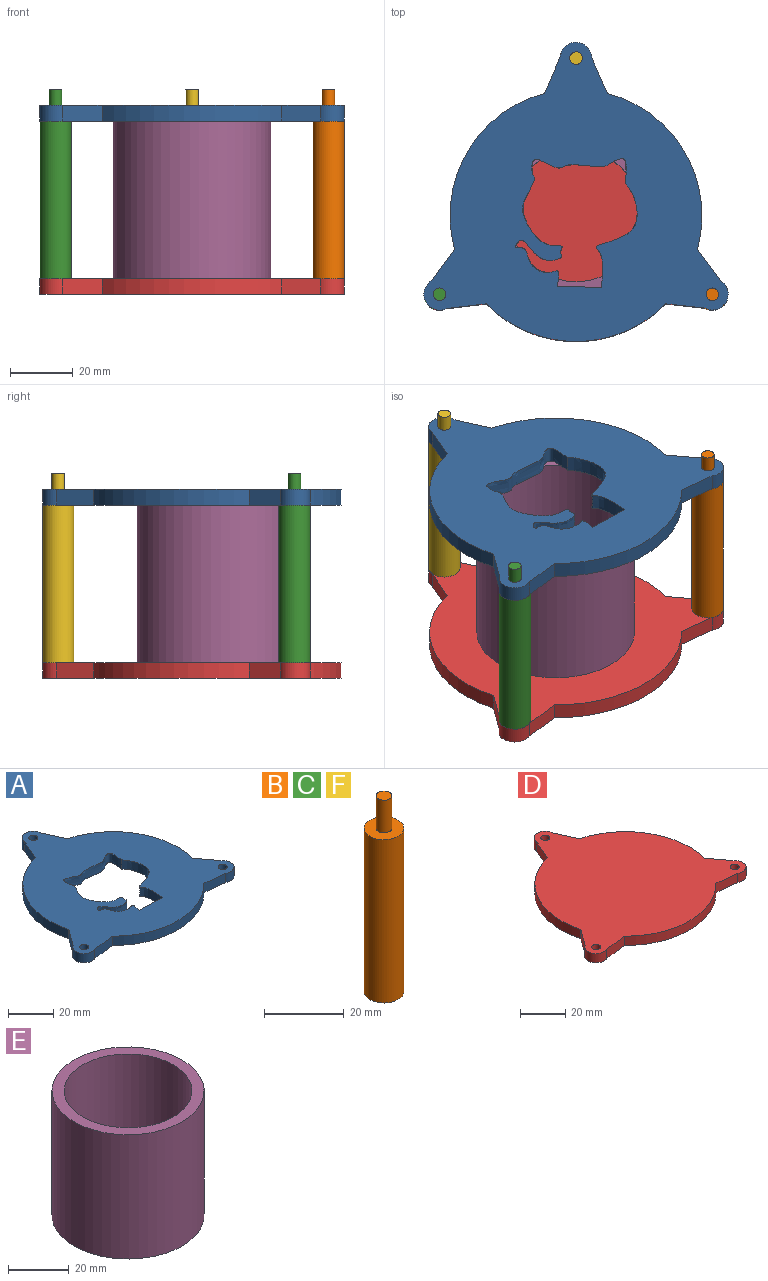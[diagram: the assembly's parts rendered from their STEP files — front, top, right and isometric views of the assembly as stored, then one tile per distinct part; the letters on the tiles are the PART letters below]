
ASSEMBLY  parts=6 mates=4
PART A: 20 faces, bbox 96.6x95x5 mm
  f0: plane 10x7.32mm, normal (-0.81,0.59,0), area 62mm2, adj f1,f17,f18,f19
  f1: cylinder r=5mm len=9.3mm, axis (0,0,-1), area 76.1mm2, adj f0,f2,f18,f19
  f2: plane 12.63x5mm, normal (0.12,-0.99,0), area 63.6mm2, adj f1,f3,f18,f19
  f3: cylinder r=40mm len=57.08mm, axis (0,0,-1), area 317.8mm2, adj f2,f4,f18,f19
  f4: plane 12.32x5mm, normal (-0.11,-0.99,0), area 62mm2, adj f3,f5,f18,f19
  f5: cylinder r=5mm len=9.11mm, axis (0,0,-1), area 76.1mm2, adj f4,f6,f18,f19
  f6: plane 10.19x7.62mm, normal (0.8,0.6,0), area 63.6mm2, adj f5,f7,f18,f19
  f7: cylinder r=40mm len=49.43mm, axis (0,0,-1), area 317.8mm2, adj f6,f8,f18,f19
  f8: plane 11.34x5mm, normal (0.91,0.4,0), area 62mm2, adj f7,f9,f18,f19
  f9: cylinder r=5mm len=9.98mm, axis (0,0,-1), area 76.1mm2, adj f8,f10,f18,f19
  f10: plane 11.69x5.02mm, normal (-0.92,0.39,0), area 63.6mm2, adj f9,f17,f18,f19
  f11: plane 14.05x5mm, normal (0.03,1,0), area 70.3mm2, adj f12,f16,f18,f19
  f12: extruded ~40.51x35.05mm, area 564.8mm2, adj f11,f16,f18,f19
  f13: cylinder r=2mm len=5mm, axis (0,0,-1), area 62.8mm2, adj f18,f19
  f14: cylinder r=2mm len=5mm, axis (0,0,-1), area 62.8mm2, adj f18,f19
  f15: cylinder r=2mm len=5mm, axis (0,0,-1), area 62.8mm2, adj f18,f19
  f16: extruded ~33.22x12.98mm, area 212.8mm2, adj f11,f12,f18,f19
  f17: cylinder r=40mm len=49.43mm, axis (0,0,-1), area 317.8mm2, adj f0,f10,f18,f19
  f18: plane 96.6x95mm, normal (0,0,1), area 4531.6mm2, adj f0,f1,f2,f3,f4,f5,f6,f7
  f19: plane 96.6x95mm, normal (0,0,-1), area 4531.6mm2, adj f0,f1,f2,f3,f4,f5,f6,f7
PART B: 7 faces, bbox 10x10x60 mm
  f0: cylinder r=5mm len=50mm, axis (0,0,-1), area 1570.8mm2, adj f1,f2
  f1: plane 10x10mm, normal (0,0,1), area 66mm2, adj f0,f3
  f2: plane 10x10mm, normal (0,0,-1), area 66mm2, adj f0,f5
  f3: cylinder r=2mm len=10mm, axis (0,0,-1), area 125.7mm2, adj f1,f4
  f4: plane 4x4mm, normal (0,0,1), area 12.6mm2, adj f3
  f5: cylinder r=2mm len=15mm, axis (0,0,-1), area 188.5mm2, adj f2,f6
  f6: plane 4x4mm, normal (0,0,-1), area 12.6mm2, adj f5
PART C: same geometry as B
PART D: 17 faces, bbox 96.6x95x5 mm
  f0: plane 10x7.32mm, normal (-0.81,0.59,0), area 62mm2, adj f1,f14,f15,f16
  f1: cylinder r=5mm len=9.3mm, axis (0,0,-1), area 76.1mm2, adj f0,f2,f15,f16
  f2: plane 12.63x5mm, normal (0.12,-0.99,0), area 63.6mm2, adj f1,f3,f15,f16
  f3: cylinder r=40mm len=57.08mm, axis (0,0,-1), area 317.8mm2, adj f2,f4,f15,f16
  f4: plane 12.32x5mm, normal (-0.11,-0.99,0), area 62mm2, adj f3,f5,f15,f16
  f5: cylinder r=5mm len=9.11mm, axis (0,0,-1), area 76.1mm2, adj f4,f6,f15,f16
  f6: plane 10.19x7.62mm, normal (0.8,0.6,0), area 63.6mm2, adj f5,f7,f15,f16
  f7: cylinder r=40mm len=49.43mm, axis (0,0,-1), area 317.8mm2, adj f6,f8,f15,f16
  f8: plane 11.34x5mm, normal (0.91,0.4,0), area 62mm2, adj f7,f9,f15,f16
  f9: cylinder r=5mm len=9.98mm, axis (0,0,-1), area 76.1mm2, adj f8,f10,f15,f16
  f10: plane 11.69x5.02mm, normal (-0.92,0.39,0), area 63.6mm2, adj f9,f14,f15,f16
  f11: cylinder r=2mm len=5mm, axis (0,0,-1), area 62.8mm2, adj f15,f16
  f12: cylinder r=2mm len=5mm, axis (0,0,-1), area 62.8mm2, adj f15,f16
  f13: cylinder r=2mm len=5mm, axis (0,0,-1), area 62.8mm2, adj f15,f16
  f14: cylinder r=40mm len=49.43mm, axis (0,0,-1), area 317.8mm2, adj f0,f10,f15,f16
  f15: plane 96.6x95mm, normal (0,0,1), area 5566.2mm2, adj f0,f1,f2,f3,f4,f5,f6,f7
  f16: plane 96.6x95mm, normal (0,0,-1), area 5566.2mm2, adj f0,f1,f2,f3,f4,f5,f6,f7
PART E: 4 faces, bbox 50x50x50 mm
  f0: cylinder r=21mm len=50mm, axis (0,0,-1), area 6597.3mm2, adj f2,f3
  f1: cylinder r=25mm len=50mm, axis (0,0,-1), area 7854mm2, adj f2,f3
  f2: plane 50x50mm, normal (0,0,1), area 578.1mm2, adj f0,f1
  f3: plane 50x50mm, normal (0,0,-1), area 578.1mm2, adj f0,f1
PART F: same geometry as B
PLACE A t=(-102.1,-77.04,-17.04)mm
PLACE B t=(-58.8,-102.04,-67.04)mm
PLACE C t=(-145.4,-102.04,-67.04)mm
PLACE D t=(-102.1,-77.04,-72.04)mm
PLACE E rot(axis=(1,0,0),180deg) t=(-102.1,-77.04,-17.04)mm
PLACE F t=(-102.1,-27.04,-67.04)mm
MATE revolute E.f1 <-> D.f7  axis (0,0,-1) through (-102.1,-77.04,-67.04)mm
MATE revolute C.f0 <-> A.f1  axis (0,0,1) through (-145.4,-102.04,-17.04)mm
MATE revolute B.f0 <-> A.f5  axis (0,0,1) through (-58.8,-102.04,-17.04)mm
MATE revolute F.f0 <-> A.f13  axis (0,0,1) through (-102.1,-27.04,-17.04)mm
